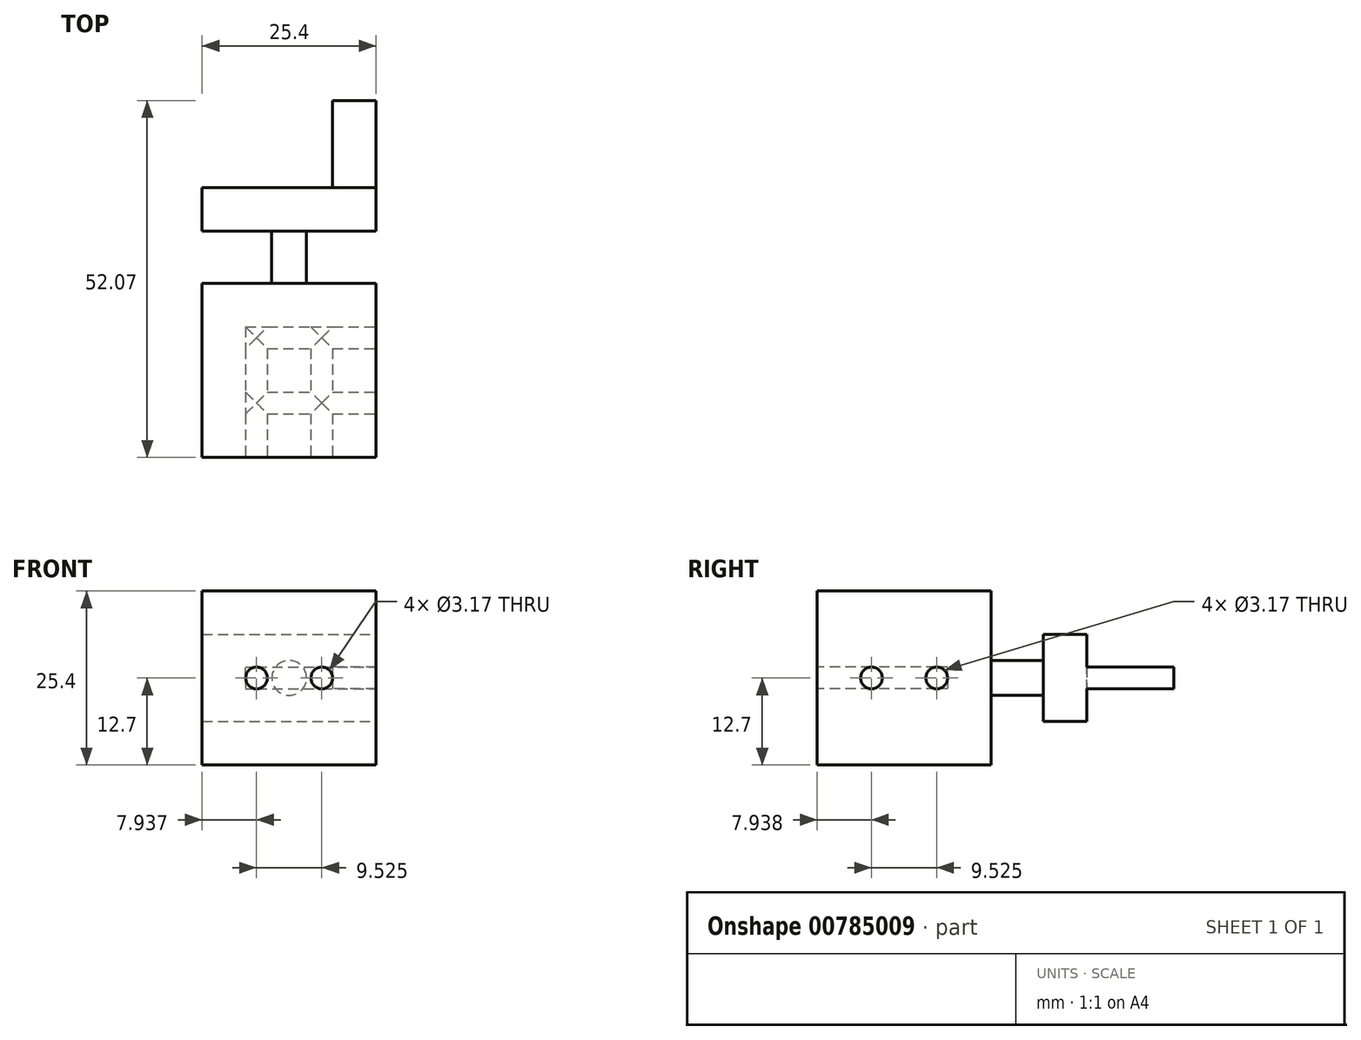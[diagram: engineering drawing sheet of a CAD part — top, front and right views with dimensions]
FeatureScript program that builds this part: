
annotation { "Feature Type Name" : "Feature", "Feature Type Description" : "" }
export const myFeature = defineFeature(function(context is Context, id is Id, definition is map)
    precondition{}
    {
        {
            var Q0;
            Q0=qCreatedBy(makeId("Front.planeOp"),FACE);
            var sketch = newSketch(context, id + "F0", { "sketchPlane" : qUnion([Q0])});
            skLineSegment(sketch, "E0.bottom", {"start": v(12.7, -12.7) * mm, "end": v(-12.7, -12.7) * mm});
            skLineSegment(sketch, "E0.top", {"start": v(12.7, 12.7) * mm, "end": v(-12.7, 12.7) * mm});
            skLineSegment(sketch, "E0.left", {"start": v(12.7, -12.7) * mm, "end": v(12.7, 12.7) * mm});
            skLineSegment(sketch, "E0.right", {"start": v(-12.7, -12.7) * mm, "end": v(-12.7, 12.7) * mm});
            skPoint(sketch, "E0.middle", {"position": v(0, 0) * mm});
            skCircle(sketch, "E1", {"center": v(4.76, 0) * mm, "radius": 1.59 * mm});
            skCircle(sketch, "E2", {"center": v(-4.76, 0) * mm, "radius": 1.59 * mm});
            skSolve(sketch);
        }
        {
            var Q0;
            Q0 = qSketchRegion(id + "F0", true);
            var Q1;
            Q1=makeQuery(id+"F0.imprint","IMPRINT",FACE,{"disambiguationData":[TD([[makeQuery(id+"F0.imprint","IMPRINT",EDGE,{"derivedFrom":sQuery(id+"F0.wireOp",EDGE,"E2")}),1.0]])]});
            var Q2;
            Q2=makeQuery(id+"F0.imprint","IMPRINT",FACE,{"disambiguationData":[TD([[makeQuery(id+"F0.imprint","IMPRINT",EDGE,{"derivedFrom":sQuery(id+"F0.wireOp",EDGE,"E1")}),1.0]])]});
            extrude(context, id + "F1", {"entities" : qUnion([Q0, Q1, Q2]), "oppositeDirection" : true, "depth" : 25.4 * mm, "offsetDistance" : 25.4 * mm});
        }
        {
            var Q0;
            Q0=makeQuery(id+"F1.opExtrude","CAP_FACE",FACE,{"disambiguationData":[OSD([sQuery(id+"F0.wireOp",EDGE,"E0.bottom"),sQuery(id+"F0.wireOp",EDGE,"E0.top"),sQuery(id+"F0.wireOp",EDGE,"E0.left"),sQuery(id+"F0.wireOp",EDGE,"E0.right")])],"isStart":false});
            var sketch = newSketch(context, id + "F2", { "sketchPlane" : qUnion([Q0])});
            skCircle(sketch, "E3", {"center": v(0, 0) * mm, "radius": 2.54 * mm});
            skSolve(sketch);
        }
        {
            var Q0;
            Q0=makeQuery(id+"F2.imprint","IMPRINT",FACE,{"disambiguationData":[TD([[makeQuery(id+"F2.imprint","IMPRINT",EDGE,{"derivedFrom":sQuery(id+"F2.wireOp",EDGE,"E3")}),1.0]])]});
            extrude(context, id + "F3", {"entities" : qUnion([Q0]), "operationType" : NewBodyOperationType.ADD, "depth" : 7.62 * mm, "offsetDistance" : 25.4 * mm});
        }
        {
            var Q0;
            Q0=makeQuery(id+"F3.opExtrude","CAP_FACE",FACE,{"disambiguationData":[OSD([sQuery(id+"F2.wireOp",EDGE,"E3")])],"isStart":false});
            var sketch = newSketch(context, id + "F4", { "sketchPlane" : qUnion([Q0])});
            skLineSegment(sketch, "E4.bottom", {"start": v(12.7, -6.35) * mm, "end": v(-12.7, -6.35) * mm});
            skLineSegment(sketch, "E4.top", {"start": v(12.7, 6.35) * mm, "end": v(-12.7, 6.35) * mm});
            skLineSegment(sketch, "E4.left", {"start": v(12.7, -6.35) * mm, "end": v(12.7, 6.35) * mm});
            skLineSegment(sketch, "E4.right", {"start": v(-12.7, -6.35) * mm, "end": v(-12.7, 6.35) * mm});
            skPoint(sketch, "E4.middle", {"position": v(0, 0) * mm});
            skSolve(sketch);
        }
        {
            var Q0;
            Q0 = qSketchRegion(id + "F4", true);
            extrude(context, id + "F5", {"entities" : qUnion([Q0]), "operationType" : NewBodyOperationType.ADD, "depth" : 6.35 * mm, "offsetDistance" : 25.4 * mm});
        }
        {
            var Q0;
            Q0=makeQuery(id+"F5.opExtrude","CAP_FACE",FACE,{"disambiguationData":[OSD([sQuery(id+"F4.wireOp",EDGE,"E4.bottom"),sQuery(id+"F4.wireOp",EDGE,"E4.top"),sQuery(id+"F4.wireOp",EDGE,"E4.left"),sQuery(id+"F4.wireOp",EDGE,"E4.right")])],"isStart":false});
            var sketch = newSketch(context, id + "F6", { "sketchPlane" : qUnion([Q0])});
            skLineSegment(sketch, "E5.bottom", {"start": v(-12.7, -1.59) * mm, "end": v(-6.35, -1.59) * mm});
            skLineSegment(sketch, "E5.top", {"start": v(-12.7, 1.59) * mm, "end": v(-6.35, 1.59) * mm});
            skLineSegment(sketch, "E5.left", {"start": v(-12.7, 1.59) * mm, "end": v(-12.7, -1.59) * mm});
            skLineSegment(sketch, "E5.right", {"start": v(-6.35, 1.59) * mm, "end": v(-6.35, -1.59) * mm});
            skSolve(sketch);
        }
        {
            var Q0;
            Q0=makeQuery(id+"F6.imprint","IMPRINT",FACE,{"disambiguationData":[TD([[makeQuery(id+"F6.imprint","IMPRINT",EDGE,{"derivedFrom":sQuery(id+"F6.wireOp",EDGE,"E5.bottom")}),1.0]])]});
            extrude(context, id + "F7", {"entities" : qUnion([Q0]), "operationType" : NewBodyOperationType.ADD, "depth" : 12.7 * mm, "offsetDistance" : 25.4 * mm});
        }
        {
            var Q0;
            Q0=makeQuery(id+"F0.imprint","IMPRINT",FACE,{"disambiguationData":[TD([[makeQuery(id+"F0.imprint","IMPRINT",EDGE,{"derivedFrom":sQuery(id+"F0.wireOp",EDGE,"E2")}),1.0]])]});
            var Q1;
            Q1=makeQuery(id+"F0.imprint","IMPRINT",FACE,{"disambiguationData":[TD([[makeQuery(id+"F0.imprint","IMPRINT",EDGE,{"derivedFrom":sQuery(id+"F0.wireOp",EDGE,"E1")}),1.0]])]});
            extrude(context, id + "F8", {"entities" : qUnion([Q0, Q1]), "operationType" : NewBodyOperationType.REMOVE, "oppositeDirection" : true, "depth" : 19.05 * mm, "offsetDistance" : 25.4 * mm});
        }
        {
            var Q0;
            Q0=makeQuery(id+"F1.opExtrude","SWEPT_FACE",FACE,{"disambiguationData":[OSD([sQuery(id+"F0.wireOp",EDGE,"E0.left")])]});
            var sketch = newSketch(context, id + "F9", { "sketchPlane" : qUnion([Q0])});
            skPoint(sketch, "E6.middle", {"position": v(12.7, 0) * mm});
            skCircle(sketch, "E7", {"center": v(17.46, 0) * mm, "radius": 1.59 * mm});
            skCircle(sketch, "E8", {"center": v(7.94, 0) * mm, "radius": 1.59 * mm});
            skSolve(sketch);
        }
        {
            var Q0;
            Q0=makeQuery(id+"F9.imprint","IMPRINT",FACE,{"disambiguationData":[TD([[makeQuery(id+"F9.imprint","IMPRINT",EDGE,{"derivedFrom":sQuery(id+"F9.wireOp",EDGE,"E8")}),1.0]])]});
            var Q1;
            Q1=makeQuery(id+"F9.imprint","IMPRINT",FACE,{"disambiguationData":[TD([[makeQuery(id+"F9.imprint","IMPRINT",EDGE,{"derivedFrom":sQuery(id+"F9.wireOp",EDGE,"E7")}),1.0]])]});
            extrude(context, id + "F10", {"entities" : qUnion([Q0, Q1]), "operationType" : NewBodyOperationType.REMOVE, "oppositeDirection" : true, "depth" : 19.05 * mm, "offsetDistance" : 25.4 * mm});
        }
    });
